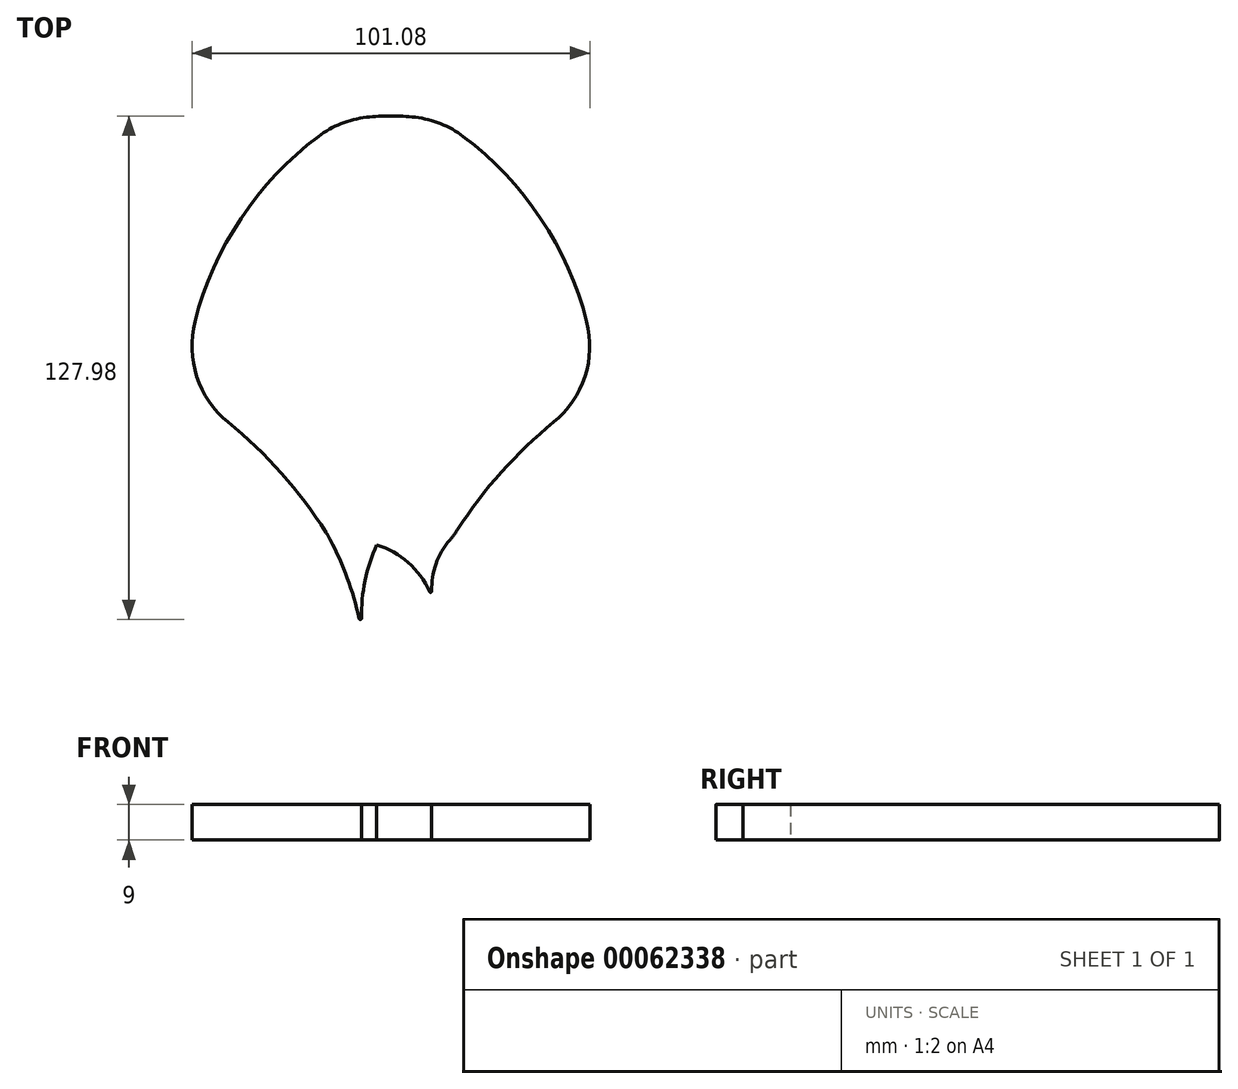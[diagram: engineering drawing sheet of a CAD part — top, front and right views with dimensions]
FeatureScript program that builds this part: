
annotation { "Feature Type Name" : "Feature", "Feature Type Description" : "" }
export const myFeature = defineFeature(function(context is Context, id is Id, definition is map)
    precondition{}
    {
        {
            var Q0;
            Q0=qCreatedBy(makeId("Top.planeOp"),FACE);
            var sketch = newSketch(context, id + "F0", { "sketchPlane" : qUnion([Q0])});
            skCircle(sketch, "E0", {"center": v(0, 0) * mm, "radius": 54.54 * mm});
            skArc(sketch, "E1", {"start": v(52.36, -15.27) * mm, "mid": v(41.12, 23.58) * mm, "end": v(13.26, 52.9) * mm});
            skArc(sketch, "E2", {"start": v(52.36, -15.27) * mm, "mid": v(32.1, -31.7) * mm, "end": v(15.93, -52.16) * mm});
            skArc(sketch, "E3.MirrorCS", {"start": v(-52.36, -15.27) * mm, "mid": v(-41.12, 23.58) * mm, "end": v(-13.26, 52.9) * mm});
            skArc(sketch, "E4.MirrorCS", {"start": v(-52.36, -15.27) * mm, "mid": v(-32.1, -31.7) * mm, "end": v(-15.93, -52.16) * mm});
            skArc(sketch, "E5", {"start": v(15.93, -52.16) * mm, "mid": v(11.36, -59.58) * mm, "end": v(10.57, -68.26) * mm});
            skArc(sketch, "E6", {"start": v(10.57, -68.26) * mm, "mid": v(5.15, -59.65) * mm, "end": v(-3.57, -54.42) * mm});
            skArc(sketch, "E7", {"start": v(-3.57, -54.42) * mm, "mid": v(-7.02, -66.27) * mm, "end": v(-7.02, -78.61) * mm});
            skArc(sketch, "E8", {"start": v(-7.02, -78.61) * mm, "mid": v(-10.34, -65) * mm, "end": v(-15.93, -52.16) * mm});
            skSolve(sketch);
        }
        {
            var Q0;
            {var subQ1=sQuery(id+"F0.wireOp",EDGE,"E1");Q0=makeQuery(id+"F0.imprint","IMPRINT",FACE,{"disambiguationData":[TD([[makeQuery(id+"F0.imprint","IMPRINT",EDGE,{"derivedFrom":subQ1}),1.0]])]});}
            extrude(context, id + "F1", {"entities" : qUnion([Q0]), "depth" : 9 * mm});
        }
        {
            var Q0;
            {var subQ2=sQuery(id+"F0.wireOp",EDGE,"E7");Q0=makeQuery(id+"F0.imprint","IMPRINT",FACE,{"disambiguationData":[TD([[makeQuery(id+"F0.imprint","IMPRINT",EDGE,{"derivedFrom":subQ2}),-1.0]])]});}
            var Q1;
            {var subQ0=sQuery(id+"F0.wireOp",EDGE,"E5");Q1=makeQuery(id+"F0.imprint","IMPRINT",FACE,{"disambiguationData":[TD([[makeQuery(id+"F0.imprint","IMPRINT",EDGE,{"derivedFrom":subQ0}),-1.0]])]});}
            extrude(context, id + "F2", {"entities" : qUnion([Q0, Q1]), "operationType" : NewBodyOperationType.ADD, "depth" : 9 * mm});
        }
        {
            var Q0;
            Q0=makeQuery(id+"F1.opExtrude","SWEPT_EDGE",EDGE,{"disambiguationData":[OSD([sQuery(id+"F0.wireOp",EDGE,"E0"),sQuery(id+"F0.wireOp",EDGE,"E1"),sQuery(id+"F0.wireOp",EDGE,"E2")])]});
            var Q1;
            Q1=makeQuery(id+"F1.opExtrude","SWEPT_EDGE",EDGE,{"disambiguationData":[OSD([sQuery(id+"F0.wireOp",EDGE,"E0"),sQuery(id+"F0.wireOp",EDGE,"E3.MirrorCS"),sQuery(id+"F0.wireOp",EDGE,"E4.MirrorCS")])]});
            var Q2;
            Q2=makeQuery(id+"F1.opExtrude","SWEPT_EDGE",EDGE,{"disambiguationData":[OSD([sQuery(id+"F0.wireOp",EDGE,"E0"),sQuery(id+"F0.wireOp",EDGE,"E2"),sQuery(id+"F0.wireOp",EDGE,"bf90f315-cd32-4384-a9ac-c9795e7612e2")])]});
            var Q3;
            Q3=makeQuery(id+"F1.opExtrude","SWEPT_EDGE",EDGE,{"disambiguationData":[OSD([sQuery(id+"F0.wireOp",EDGE,"E0"),sQuery(id+"F0.wireOp",EDGE,"E4.MirrorCS"),sQuery(id+"F0.wireOp",EDGE,"87501752-9129-4e11-a6c5-649eff0720900.MirrorCS")])]});
            var Q4;
            Q4=makeQuery(id+"F1.opExtrude","SWEPT_EDGE",EDGE,{"disambiguationData":[OSD([sQuery(id+"F0.wireOp",EDGE,"E0"),sQuery(id+"F0.wireOp",EDGE,"E1")])]});
            var Q5;
            Q5=makeQuery(id+"F1.opExtrude","SWEPT_EDGE",EDGE,{"disambiguationData":[OSD([sQuery(id+"F0.wireOp",EDGE,"E0"),sQuery(id+"F0.wireOp",EDGE,"E3.MirrorCS")])]});
            fillet(context, id + "F3", {"entities" : qUnion([Q0, Q1, Q2, Q3, Q4, Q5]), "radius" : 25 * mm, "tangentPropagation" : true, "allowEdgeOverflow" : false});
        }
        {
            var Q0;
            Q0=makeQuery(id+"F2.opExtrude","SWEPT_EDGE",EDGE,{"disambiguationData":[OSD([sQuery(id+"F0.wireOp",EDGE,"E7"),sQuery(id+"F0.wireOp",EDGE,"E8")])]});
            var Q1;
            Q1=makeQuery(id+"F2.opExtrude","SWEPT_EDGE",EDGE,{"disambiguationData":[OSD([sQuery(id+"F0.wireOp",EDGE,"E5"),sQuery(id+"F0.wireOp",EDGE,"E6")])]});
            fillet(context, id + "F4", {"entities" : qUnion([Q0, Q1]), "radius" : 0.3 * mm, "tangentPropagation" : true, "allowEdgeOverflow" : false});
        }
    });
